# Revit family: PGR_Noken_WtrSplyFitngsForWshBsnsAndTrghs_Tono-E
name_source: partatom
category: Plumbing Fixtures
revit_build: Autodesk Revit 2017 (Build: 20190508_0315(x64)
units: mm (PartAtom-declared; Revit-internal decimal feet)

## family parameters
Always vertical = Yes
Cut with Voids When Loaded = No
OmniClass Number = 23.45.55.17
OmniClass Title = Mixing Faucets
Part Type = Normal
Room Calculation Point = No
Round Connector Dimension = Use Diameter
Shared = No
Work Plane-Based = Yes

## types (1)
- Tono-100184771
    AccessibilityPerformance = WaterSupplyFittingsForWashBasinsAndTroughs_Tono_Chrome-30x140x108mm-100184771
    AssetType = Cold
    BIMObjectName = Brass
    Category = Pillar
    CloseOffRating = 0.0 Pa
    CodePerformance = Pr_40_20_87_98: Washbasin taps
    Collection = 45-35-70/371
    Color = 30x140x108mm
    Constituents = Single lever sensor mixer 3/8”. Length of hoses 400 mm. Without pop-up waste. Flow rate 6,8 l/min. at 3 bar. Material brass, finish chrome plated. 5 years warranty for superficial finishes and 2 years for the rest of components. EN 15091, EN 817, EN 248
    Default Elevation = 0 mm  [stored 0 ft]
    Description = Other
    DurationUnit = Fixed
    Features = 100184771
    FlowCoefficient = 0
    Grade = See ProductInformation for technical PDF
    IfcExportAs = IfcValveType
    IfcExportType = Faucet
    InletConnectionSize = 0 mm  [stored 0 ft]
    Manufacturer = Chrome
    ManufacturerURL = 1900-12-31T23:59:59
    Material = 6,8
    MaterialMetal = PGR_Noken_Brass_Chrome
    MaterialPlastic = PGR_Noken_Plastic_Black
    Model = 100184771
    ModelNumber = Electronic
    ModelReference = EN 15091, EN 817, EN 248
    NBSDescription = 1900-12-31T23:59:59
    Name = 0
    NettWeight = 0
    NominalHeight = 108 mm  [stored 0.354331 ft]
    NominalLength = 110 mm  [stored 0.360892 ft]
    NominalWidth = 30 mm  [stored 0.0984252 ft]
    NumberOfConnections = 0
    OutletConnectionSize = 0 mm  [stored 0 ft]
    Reference = -
    Shape = year
    Status = Unset
    SustainabilityPerformance = See ProductInformation for technical PDF
    TestPressure = 0.0 Pa
    Type Image = 100184771.jpg
    URL = www.noken.com
    Uniclass2015Title = Porcelanosa Group
    Uniclass2015Version = PGR_Noken_WaterSupplyFittingsForWashBasinsAndTroughs_Tono_Chrome-30x140x108mm-100184771
    Version = http://calidad.info-grupo.com:8081
    WarrantyDurationLabor = GRIFERIA SENSOR TONO LAVABO CROMO
    WarrantyDurationParts = 108
    WarrantyDurationUnit = 140
    WarrantyGuarantorLabor = 30

note: [stored X ft] marks values corroborated as IEEE doubles in the binary element streams (Revit-internal decimal feet)

## geometry (parser evidence)
native form markers: Blend x2, Sweep x2
no freeform markers — native parametric forms only
